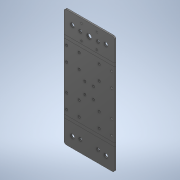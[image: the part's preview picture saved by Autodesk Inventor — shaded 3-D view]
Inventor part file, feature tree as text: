
AUTODESK INVENTOR PART (.ipt)
format: ipt  version: 2020 (Build 240168000, 168)  size: 256,000 bytes
history: native  units: mm
features: sketch x7, other x7, sheet_metal_op x5, fillet x1, pattern_linear x1
ambient origin geometry x8: Origin, YZ Plane, XZ Plane, XY Plane, X Axis, Y Axis, Z Axis, Center Point
bodies: Solid1 (feature_tree)
feature tree (21):
  sheet_metal_op  "Face1"
  sheet_metal_op  "Flange1"
  fillet  "Fillet1"  Radius=105.0mm
  pattern_linear  "Rectangular Pattern1"  Count1=15  [1 undecoded]
  sheet_metal_op  "Unfold1"
  sketch  "Sketch1"  dims[d2=3.0mm]
  other  "Plate1"
  sketch  "Sketch2"  dims[d3=3.0mm]
  other  "Plate2"
  sheet_metal_op  "Bend1"
  sheet_metal_op  "Corner1"
  sketch  "Sketch3"  dims[d4=1.5mm]
  sketch  "Sketch4"  dims[d5=6.0mm]
  sketch  "Sketch5"  dims[d6=3.0mm]
  sketch  "Sketch6"  dims[d7=53.0mm d8=90.0deg d9=3.0mm]
  sketch  "Sketch7"  dims[d10=12.0mm d11=3.0mm d12=3.0mm d13=8.3mm d14=8.3mm d15=70.0mm d16=35.0mm d17=22.0mm d18=22.0mm d19=3.0mm d20=0.0mm d21=37.0mm d22=18.5mm d23=6.5mm d24=6.5mm d25=25.0mm d26=25.0mm d27=3.0mm d28=0.0mm d29=4.0mm d30=32.0mm d31=32.0mm d32=0.0mm d33=25.0mm d34=3.5mm d35=3.5mm d36=3.5mm d37=3.5mm d38=10.0mm d39=3.0mm d40=0.0mm d41=6.5mm d42=6.5mm d43=25.0mm d44=25.0mm d45=37.0mm d46=18.5mm d47=30.5mm d48=26.0mm d49=4.5mm d50=4.5mm d51=4.5mm d52=4.5mm d53=43.0mm d54=34.0mm d55=3.0mm d56=0.0mm d57=20.0mm d59=68.0mm d60=20.0mm d62=86.0mm d63=24.0mm d64=18.0mm d65=4.5mm d66=4.5mm d67=4.5mm d68=4.5mm d69=3.0mm d70=0.0mm]
  other  "Cut1"
  other  "Cut2"
  other  "Cut3"
  other  "Cut4"
  other  "Cut5"
note: 1 required parameter value undecoded (feature->parameter linkage not recoverable at this tier; creation-order binding heuristic only, values carry confidence <= 0.55)
